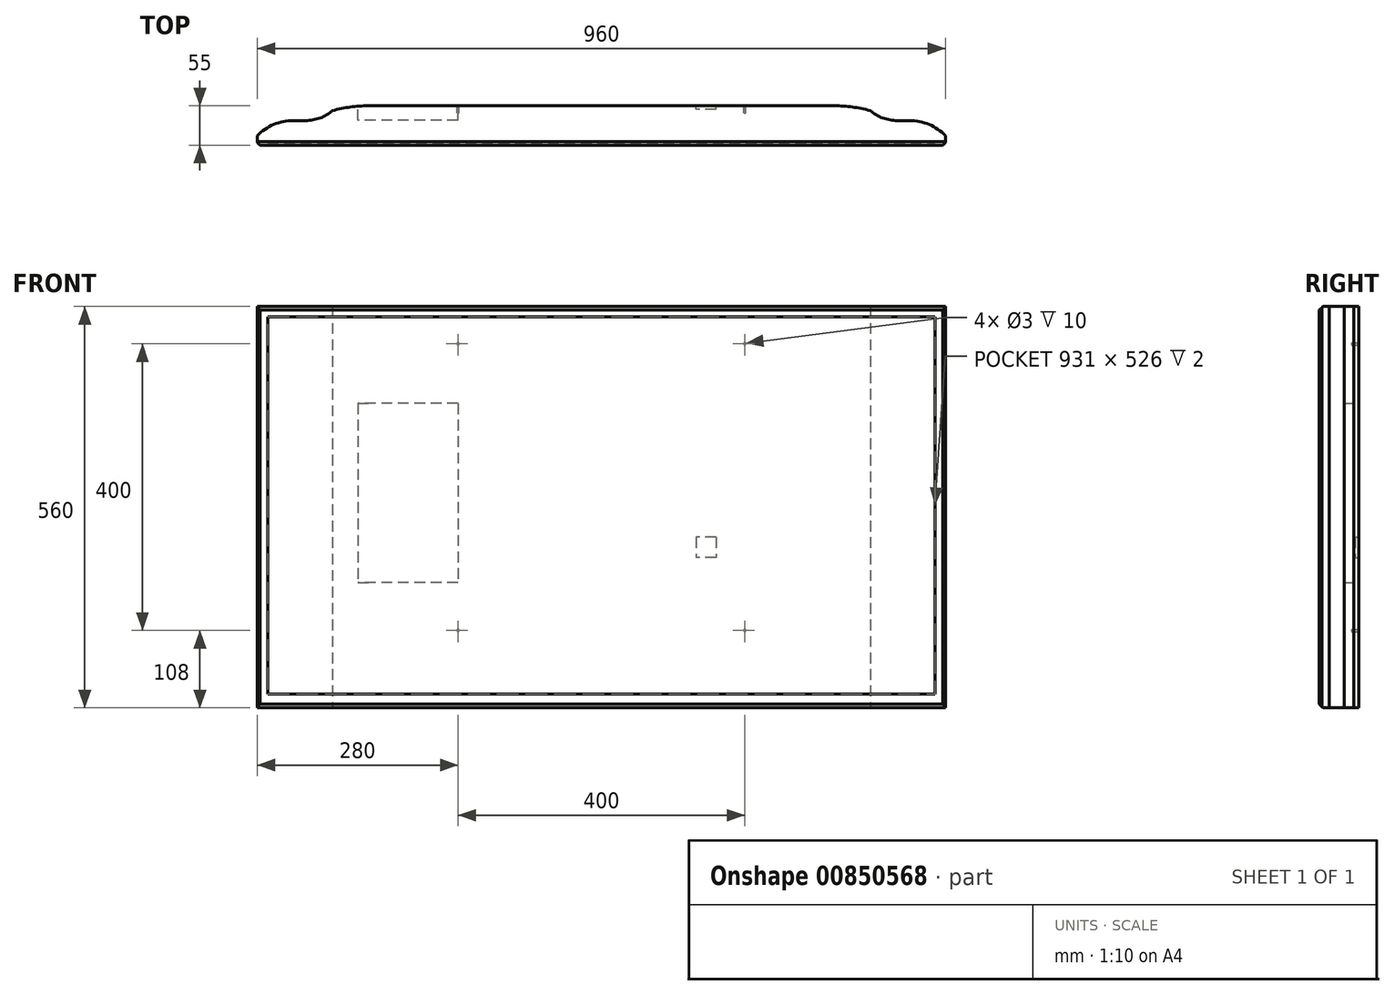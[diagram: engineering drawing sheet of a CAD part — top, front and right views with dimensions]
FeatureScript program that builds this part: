
annotation { "Feature Type Name" : "Feature", "Feature Type Description" : "" }
export const myFeature = defineFeature(function(context is Context, id is Id, definition is map)
    precondition{}
    {
        {
            var Q0;
            Q0=qCreatedBy(makeId("Top.planeOp"),FACE);
            var sketch = newSketch(context, id + "F0", { "sketchPlane" : qUnion([Q0])});
            skLineSegment(sketch, "E0", {"start": v(-476.46, -27.5) * mm, "end": v(-480, -23.96) * mm});
            skLineSegment(sketch, "E1", {"start": v(-480, -23.96) * mm, "end": v(-480, -14.01) * mm});
            skArc(sketch, "E2", {"start": v(-480, -14.01) * mm, "mid": v(-457.12, 1.53) * mm, "end": v(-430, 7) * mm});
            skLineSegment(sketch, "E3", {"start": v(-430, 7) * mm, "end": v(-412.5, 7) * mm});
            skArc(sketch, "E4", {"start": v(-412.5, 7) * mm, "mid": v(-392.52, 10.56) * mm, "end": v(-375, 20.8) * mm});
            skLineSegment(sketch, "E5", {"start": v(0, 27.5) * mm, "end": v(0, -27.5) * mm});
            skLineSegment(sketch, "E6", {"start": v(-476.46, -27.5) * mm, "end": v(0, -27.5) * mm});
            skArc(sketch, "E7", {"start": v(-375, 20.8) * mm, "mid": v(-350.22, 25.82) * mm, "end": v(-325, 27.5) * mm});
            skLineSegment(sketch, "E8", {"start": v(-325, 27.5) * mm, "end": v(0, 27.5) * mm});
            skLineSegment(sketch, "E9", {"start": v(0, 120.4) * mm, "end": v(0, -101.14) * mm, "construction": true});
            skLineSegment(sketch, "E10.MirrorCS", {"start": v(325, 27.5) * mm, "end": v(0, 27.5) * mm});
            skArc(sketch, "E11.MirrorCS", {"start": v(375, 20.8) * mm, "mid": v(350.22, 25.82) * mm, "end": v(325, 27.5) * mm});
            skArc(sketch, "E12.MirrorCS", {"start": v(412.5, 7) * mm, "mid": v(392.52, 10.56) * mm, "end": v(375, 20.8) * mm});
            skLineSegment(sketch, "E13.MirrorCS", {"start": v(430, 7) * mm, "end": v(412.5, 7) * mm});
            skArc(sketch, "E14.MirrorCS", {"start": v(480, -14.01) * mm, "mid": v(457.12, 1.53) * mm, "end": v(430, 7) * mm});
            skLineSegment(sketch, "E15.MirrorCS", {"start": v(480, -23.96) * mm, "end": v(480, -14.01) * mm});
            skLineSegment(sketch, "E16.MirrorCS", {"start": v(476.46, -27.5) * mm, "end": v(480, -23.96) * mm});
            skLineSegment(sketch, "E17.MirrorCS", {"start": v(476.46, -27.5) * mm, "end": v(0, -27.5) * mm});
            skSolve(sketch);
        }
        {
            var Q0;
            Q0=makeQuery(id+"F0.imprint","IMPRINT",FACE,{"disambiguationData":[TD([[makeQuery(id+"F0.imprint","IMPRINT",EDGE,{"derivedFrom":sQuery(id+"F0.wireOp",EDGE,"E0")}),-1.0]])]});
            var Q1;
            Q1=makeQuery(id+"F0.imprint","IMPRINT",FACE,{"disambiguationData":[TD([[makeQuery(id+"F0.imprint","IMPRINT",EDGE,{"derivedFrom":sQuery(id+"F0.wireOp",EDGE,"E5")}),1.0]])]});
            extrude(context, id + "F1", {"entities" : qUnion([Q0, Q1]), "endBound" : BoundingType.SYMMETRIC, "depth" : 560 * mm, "offsetDistance" : 25 * mm});
        }
        {
            var Q0;
            Q0=makeQuery(id+"F1.opExtrude","CAP_EDGE",EDGE,{"disambiguationData":[OSD([sQuery(id+"F0.wireOp",EDGE,"E6"),sQuery(id+"F0.wireOp",EDGE,"E17.MirrorCS")])],"isStart":false});
            var Q1;
            Q1=makeQuery(id+"F1.opExtrude","CAP_EDGE",EDGE,{"disambiguationData":[OSD([sQuery(id+"F0.wireOp",EDGE,"E6"),sQuery(id+"F0.wireOp",EDGE,"E17.MirrorCS")])],"isStart":true});
            chamfer(context, id + "F2", {"entities" : qUnion([Q0, Q1]), "width" : 5 * mm, "tangentPropagation" : true});
        }
        {
            var Q0;
            Q0=makeQuery(id+"F1.opExtrude","SWEPT_FACE",FACE,{"disambiguationData":[OSD([sQuery(id+"F0.wireOp",EDGE,"E6"),sQuery(id+"F0.wireOp",EDGE,"E17.MirrorCS")])]});
            var sketch = newSketch(context, id + "F3", { "sketchPlane" : qUnion([Q0])});
            skLineSegment(sketch, "E18.bottom", {"start": v(-465.5, 265.5) * mm, "end": v(465.5, 265.5) * mm});
            skLineSegment(sketch, "E18.top", {"start": v(-465.5, -260.5) * mm, "end": v(465.5, -260.5) * mm});
            skLineSegment(sketch, "E18.left", {"start": v(-465.5, 265.5) * mm, "end": v(-465.5, -260.5) * mm});
            skLineSegment(sketch, "E18.right", {"start": v(465.5, 265.5) * mm, "end": v(465.5, -260.5) * mm});
            skSolve(sketch);
        }
        {
            var Q0;
            Q0 = qSketchRegion(id + "F3", true);
            extrude(context, id + "F4", {"entities" : qUnion([Q0]), "operationType" : NewBodyOperationType.REMOVE, "oppositeDirection" : true, "depth" : 2 * mm, "offsetDistance" : 25 * mm});
        }
        {
            var Q0;
            Q0=makeQuery(id+"F1.opExtrude","SWEPT_FACE",FACE,{"disambiguationData":[OSD([sQuery(id+"F0.wireOp",EDGE,"E8"),sQuery(id+"F0.wireOp",EDGE,"E10.MirrorCS")])]});
            var sketch = newSketch(context, id + "F5", { "sketchPlane" : qUnion([Q0])});
            skCircle(sketch, "E19", {"center": v(200, -172) * mm, "radius": 1.5 * mm});
            skCircle(sketch, "E20", {"center": v(200, 228) * mm, "radius": 1.5 * mm});
            skCircle(sketch, "E21", {"center": v(-200, 228) * mm, "radius": 1.5 * mm});
            skCircle(sketch, "E22", {"center": v(-200, -172) * mm, "radius": 1.5 * mm});
            skSolve(sketch);
        }
        {
            var Q0;
            Q0=makeQuery(id+"F5.imprint","IMPRINT",FACE,{"disambiguationData":[TD([[makeQuery(id+"F5.imprint","IMPRINT",EDGE,{"derivedFrom":sQuery(id+"F5.wireOp",EDGE,"E21")}),1.0]])]});
            var Q1;
            Q1=makeQuery(id+"F5.imprint","IMPRINT",FACE,{"disambiguationData":[TD([[makeQuery(id+"F5.imprint","IMPRINT",EDGE,{"derivedFrom":sQuery(id+"F5.wireOp",EDGE,"E20")}),1.0]])]});
            var Q2;
            Q2=makeQuery(id+"F5.imprint","IMPRINT",FACE,{"disambiguationData":[TD([[makeQuery(id+"F5.imprint","IMPRINT",EDGE,{"derivedFrom":sQuery(id+"F5.wireOp",EDGE,"E19")}),1.0]])]});
            var Q3;
            Q3=makeQuery(id+"F5.imprint","IMPRINT",FACE,{"disambiguationData":[TD([[makeQuery(id+"F5.imprint","IMPRINT",EDGE,{"derivedFrom":sQuery(id+"F5.wireOp",EDGE,"E22")}),1.0]])]});
            extrude(context, id + "F6", {"entities" : qUnion([Q0, Q1, Q2, Q3]), "operationType" : NewBodyOperationType.REMOVE, "oppositeDirection" : true, "depth" : 10 * mm, "offsetDistance" : 25 * mm});
        }
        {
            var Q0;
            Q0=makeQuery(id+"F1.opExtrude","SWEPT_FACE",FACE,{"disambiguationData":[OSD([sQuery(id+"F0.wireOp",EDGE,"E8"),sQuery(id+"F0.wireOp",EDGE,"E10.MirrorCS")])]});
            var sketch = newSketch(context, id + "F7", { "sketchPlane" : qUnion([Q0])});
            skLineSegment(sketch, "E23.bottom", {"start": v(200, 145) * mm, "end": v(340, 145) * mm});
            skLineSegment(sketch, "E23.top", {"start": v(200, -105) * mm, "end": v(340, -105) * mm});
            skLineSegment(sketch, "E23.left", {"start": v(200, 145) * mm, "end": v(200, -105) * mm});
            skLineSegment(sketch, "E23.right", {"start": v(340, 145) * mm, "end": v(340, -105) * mm});
            skSolve(sketch);
        }
        {
            var Q0;
            {var subQ0=sQuery(id+"F7.wireOp",EDGE,"E23.right");Q0=makeQuery(id+"F7.imprint","IMPRINT",FACE,{"disambiguationData":[TD([[makeQuery(id+"F7.imprint","IMPRINT",EDGE,{"derivedFrom":subQ0}),-1.0]])]});}
            var Q1;
            {var subQ0=sQuery(id+"F7.wireOp",EDGE,"E23.left");Q1=makeQuery(id+"F7.imprint","IMPRINT",FACE,{"disambiguationData":[TD([[makeQuery(id+"F7.imprint","IMPRINT",EDGE,{"derivedFrom":subQ0}),1.0]])]});}
            extrude(context, id + "F8", {"entities" : qUnion([Q0, Q1]), "operationType" : NewBodyOperationType.REMOVE, "oppositeDirection" : true, "depth" : 20 * mm, "offsetDistance" : 25 * mm});
        }
        {
            var Q0;
            Q0=makeQuery(id+"F1.opExtrude","SWEPT_FACE",FACE,{"disambiguationData":[OSD([sQuery(id+"F0.wireOp",EDGE,"E8"),sQuery(id+"F0.wireOp",EDGE,"E10.MirrorCS")])]});
            var sketch = newSketch(context, id + "F9", { "sketchPlane" : qUnion([Q0])});
            skLineSegment(sketch, "E24.bottom", {"start": v(-160, -42) * mm, "end": v(-132, -42) * mm});
            skLineSegment(sketch, "E24.top", {"start": v(-160, -70) * mm, "end": v(-132, -70) * mm});
            skLineSegment(sketch, "E24.left", {"start": v(-160, -42) * mm, "end": v(-160, -70) * mm});
            skLineSegment(sketch, "E24.right", {"start": v(-132, -42) * mm, "end": v(-132, -70) * mm});
            skSolve(sketch);
        }
        {
            var Q0;
            Q0=makeQuery(id+"F9.imprint","IMPRINT",FACE,{"disambiguationData":[TD([[makeQuery(id+"F9.imprint","IMPRINT",EDGE,{"derivedFrom":sQuery(id+"F9.wireOp",EDGE,"E24.bottom")}),-1.0]])]});
            extrude(context, id + "F10", {"entities" : qUnion([Q0]), "operationType" : NewBodyOperationType.REMOVE, "oppositeDirection" : true, "depth" : 5 * mm, "offsetDistance" : 25 * mm});
        }
    });
